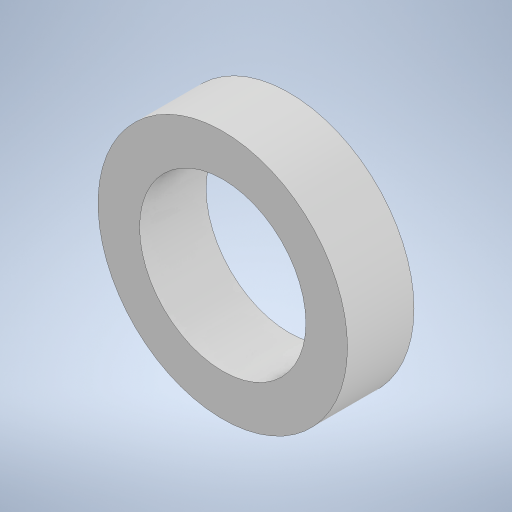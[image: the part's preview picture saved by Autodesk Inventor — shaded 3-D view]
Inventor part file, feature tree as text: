
AUTODESK INVENTOR PART (.ipt)
format: ipt  version: 2023 (Build 270158000, 158)  size: 222,720 bytes
history: native  units: mm
features: extrude x2, sketch x2, other x1
ambient origin geometry x8: Origin, YZ Plane, XZ Plane, XY Plane, X Axis, Y Axis, Z Axis, Center Point
bodies: Body1 (feature_tree)
feature tree (5):
  other  "Твердое тело1"
  extrude  "Выдавливание1"  Depth=15.0mm
  extrude  "Выдавливание2"  Depth=4.0mm TaperAngle=0.0deg
  sketch  "Эскиз1"
  sketch  "Эскиз2"
